# Revit family: Lighting_Fixture-Wall-Astro-Bloc
name_source: partatom
category: Lighting Fixtures
revit_build: Autodesk Revit 2018 (Build: 20170223_1515(x64)
units: mm (PartAtom-declared; Revit-internal decimal feet)

## family parameters
Cut with Voids When Loaded = No
Host = Face
Light Source = Yes
OmniClass Number = 23.80.70.00
OmniClass Title = Lighting
Part Type = Normal
Room Calculation Point = No
Round Connector Dimension = Use Diameter
Shared = No

## types (4) — shared parameters
Apparent Load = 3 VA
Assembly Code = D5020200
Class = 2
Color Filter = 16777215
Description = Wall Light
Dimmable = No
Dimming Lamp Color Temperature Shift = <None>
Energy Efficiency Rating = A
Height = 100 mm  [stored 0.328084 ft]
IP Rating = IP44
Lamp = LED
Lamp included = Integrated
Length = 50 mm  [stored 0.164042 ft]
Light Source From Wall = 33 mm  [stored 0.108268 ft]
Luminaire Lamp Efficiency Rating = A
Manufacturer = Astro Lighting Ltd, CM20 2DP
Mountable on normally flammable surfaces = Yes
Number of Poles = 1
Photometric Web File = 0829 BLOC CHROME.ies
Product Documentation = http://www.astrolighting.co.uk
Suitable for bathroom zone = Zones 2 and 3
Tilt Angle = 0.00°
Type Comments = Can be mounted horizontally or vertically
URL = www.astrolighting.co.uk
Voltage = 230 V
Wattage Comments = 2 x 1w
Weight = 1.2kg
Width = 35 mm  [stored 0.114829 ft]

## per-type parameters (varying)
| type | Casing Material | Model |
| 0829 Bloc (Polished Chrome) | Astro - Zinc - Chrome Finish | 0829 Bloc Polished Chrome |
| 0824 Bloc (Matt Nickel) | Astro - Zinc - Matt Nickel | 0824 Bloc Matt Nickel |
| 7044 Bloc (Silver) | Astro - Zinc - Silver Paint | 7044 Bloc Painted Silver |
| 7275 Bloc (White) | Astro - Zinc - White | 7275 Bloc White |

note: [stored X ft] marks values corroborated as IEEE doubles in the binary element streams (Revit-internal decimal feet)

## geometry (parser evidence)
native form markers: Sweep x1
no freeform markers — native parametric forms only
